# Revit family: Toilet-Siphon_Jet-Whitehall-BestCare-WH2145ADA_Series
name_source: partatom
category: Plumbing Fixtures
units: mm (PartAtom-declared; Revit-internal decimal feet)

## family parameters
Cut with Voids When Loaded = No
Host = Face
OmniClass Number = 23.45.05.21.11.11
OmniClass Title = Water Operated Water Closets
Part Type = Normal
Room Calculation Point = No
Round Connector Dimension = Use Diameter
Shared = Yes

## types (2) — shared parameters
ADA Compliant = Yes
Assembly Code = D2010110
Bowl Shape = Elongated
CW Connection = Yes
CWFU = 10
Connection Diameter = 7/8"
Default Elevation = 0"
Description = BestCare® Ligature-Resistant Cistern Tank Toilet with ADA Seat Height
Finish = Stainless Steel-Whitehall-Powder Coated White
Flush Rate = 1.28 gallons (4.8 Liters) to 1.6 gallons (6 liter) per flush
HW Connection = No
Height = 35 1/4"
IAPMO Compliance = Toilet shall be ASME A112.19.3 and CSA B45.4 compliant.
Installation Type = Floor Mounted
Length = 30 1/2"
Load Capacity = On-floor units can withstand load rating of 5000 lbs.
Manufacturer = Whitehall Mfg.
Material = Stainless Steel-Whitehall-Powder Coated White
Product Documentation Link = https://www.whitehallmfg.com
Product Page URL = https://www.whitehallmfg.com
URL = http://www.whitehallmfg.com
Vent Connection = No
WFU = 10
WH-LRSC-BLACK-Ligature Resistant Seat Cover, Black (Shipped Loose = No
WH-LRSC-GRAY-Whitehall Ligature Resistant ABS Toilet Seat Cover = Yes
WH-LRSC-WHITE-Ligature Resistant Seat Cover, White (Shipped Loose = No
Waste Connection = Yes
Waste Connection Diameter = 7 1/2"
Width = 17 1/8"
zero-valued in all types: HWFU

## per-type parameters (varying)
| type | Waste Connection Distance From Wall |
| WH2145ADA_10 | 10" |
| WH2145ADA_12 | 12" |

note: column(s) folded — value = type name in every type: Model

## geometry (parser evidence)
native form markers: Sweep x2
no freeform markers — native parametric forms only
